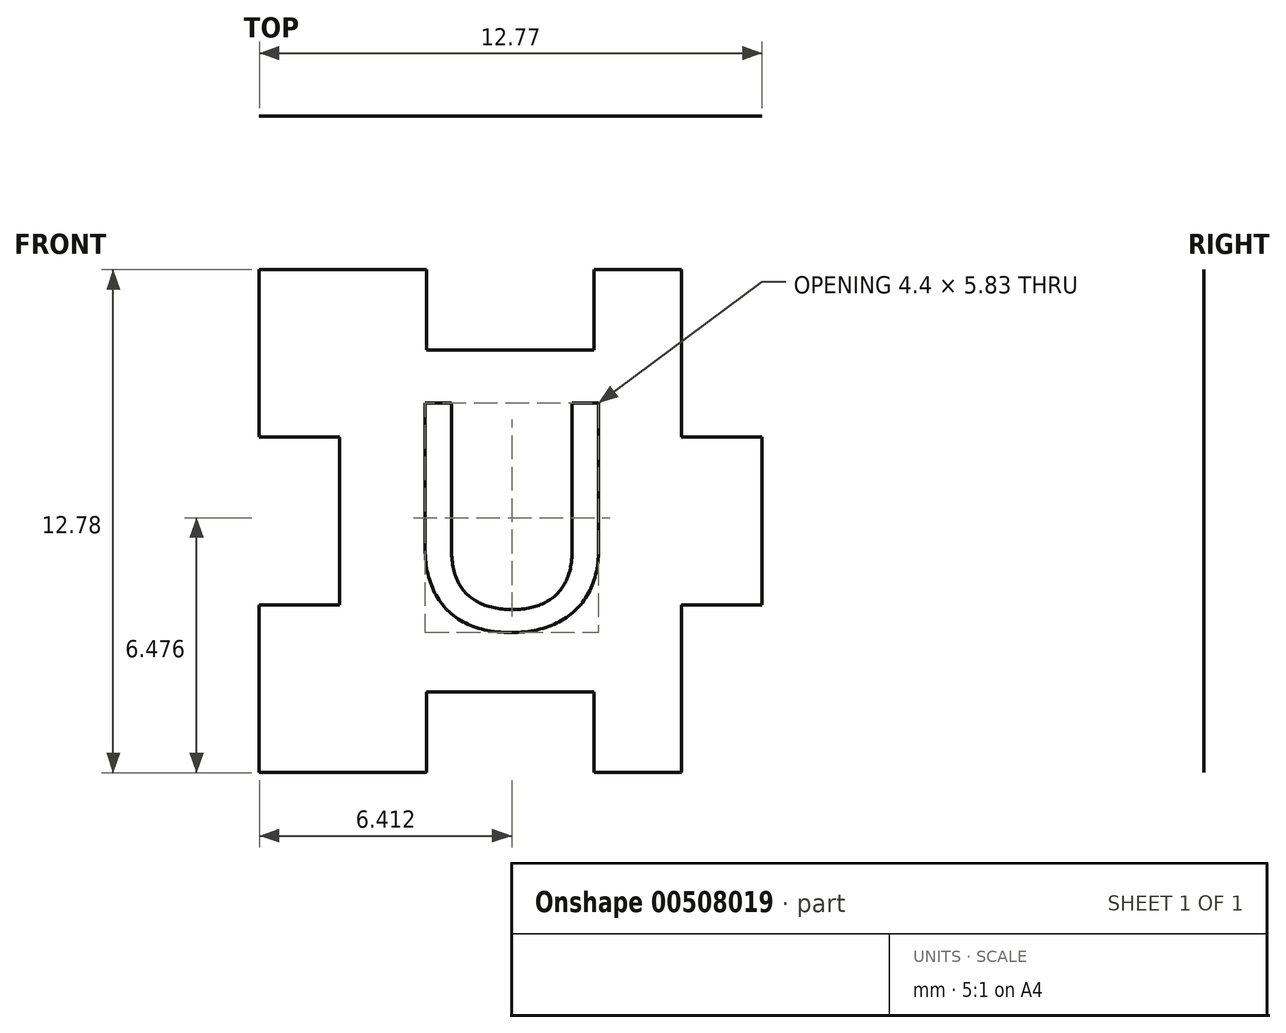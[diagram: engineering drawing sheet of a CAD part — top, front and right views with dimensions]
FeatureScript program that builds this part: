
annotation { "Feature Type Name" : "Feature", "Feature Type Description" : "" }
export const myFeature = defineFeature(function(context is Context, id is Id, definition is map)
    precondition{}
    {
        {
            var Q0;
            Q0=qCreatedBy(makeId("Front.planeOp"),FACE);
            var sketch = newSketch(context, id + "F0", { "sketchPlane" : qUnion([Q0])});
            skLineSegment(sketch, "E0", {"start": v(-10.99, 26.89) * mm, "end": v(-10.99, 29.02) * mm});
            skLineSegment(sketch, "E1", {"start": v(-10.99, 29.02) * mm, "end": v(-13.03, 29.02) * mm});
            skLineSegment(sketch, "E2", {"start": v(-13.03, 29.02) * mm, "end": v(-13.03, 33.28) * mm});
            skLineSegment(sketch, "E3", {"start": v(-13.03, 33.28) * mm, "end": v(-8.78, 33.28) * mm});
            skLineSegment(sketch, "E4", {"start": v(-8.78, 33.28) * mm, "end": v(-8.78, 31.23) * mm});
            skLineSegment(sketch, "E5", {"start": v(-8.78, 31.23) * mm, "end": v(-4.53, 31.23) * mm});
            skLineSegment(sketch, "E6", {"start": v(-4.53, 31.23) * mm, "end": v(-4.53, 33.28) * mm});
            skLineSegment(sketch, "E7", {"start": v(-4.53, 33.28) * mm, "end": v(-2.3, 33.28) * mm});
            skLineSegment(sketch, "E8", {"start": v(-2.3, 33.28) * mm, "end": v(-2.3, 29.02) * mm});
            skLineSegment(sketch, "E9", {"start": v(-2.3, 29.02) * mm, "end": v(-0.26, 29.02) * mm});
            skLineSegment(sketch, "E10", {"start": v(-10.99, 26.89) * mm, "end": v(8.72, 26.89) * mm, "construction": true});
            skLineSegment(sketch, "E11.MirrorCS", {"start": v(-2.3, 24.76) * mm, "end": v(-0.26, 24.76) * mm});
            skLineSegment(sketch, "E12.MirrorCS", {"start": v(-2.3, 20.5) * mm, "end": v(-2.3, 24.76) * mm});
            skLineSegment(sketch, "E13.MirrorCS", {"start": v(-4.53, 20.5) * mm, "end": v(-2.3, 20.5) * mm});
            skLineSegment(sketch, "E14.MirrorCS", {"start": v(-4.53, 22.55) * mm, "end": v(-4.53, 20.5) * mm});
            skLineSegment(sketch, "E15.MirrorCS", {"start": v(-8.78, 22.55) * mm, "end": v(-4.53, 22.55) * mm});
            skLineSegment(sketch, "E16.MirrorCS", {"start": v(-8.78, 20.5) * mm, "end": v(-8.78, 22.55) * mm});
            skLineSegment(sketch, "E17.MirrorCS", {"start": v(-13.03, 20.5) * mm, "end": v(-8.78, 20.5) * mm});
            skLineSegment(sketch, "E18.MirrorCS", {"start": v(-13.03, 24.76) * mm, "end": v(-13.03, 20.5) * mm});
            skLineSegment(sketch, "E19.MirrorCS", {"start": v(-10.99, 24.76) * mm, "end": v(-13.03, 24.76) * mm});
            skLineSegment(sketch, "E20.MirrorCS", {"start": v(-10.99, 26.89) * mm, "end": v(-10.99, 24.76) * mm});
            skLineSegment(sketch, "E21", {"start": v(-0.26, 29.02) * mm, "end": v(-0.26, 24.76) * mm});
            skSolve(sketch);
        }
        {
            var Q0;
            Q0=makeQuery(id+"F0.imprint","IMPRINT",FACE,{"disambiguationData":[TD([[makeQuery(id+"F0.imprint","IMPRINT",EDGE,{"derivedFrom":sQuery(id+"F0.wireOp",EDGE,"E0")}),-1.0]])]});
            extrude(context, id + "F1", {"entities" : qUnion([Q0]), "depth" : .16 / 50.8 * mm, "offsetDistance" : 25 * mm});
        }
        {
            var Q0;
            Q0=makeQuery(id+"F1.opExtrude","CAP_FACE",FACE,{"disambiguationData":[OSD([sQuery(id+"F0.wireOp",EDGE,"E0"),sQuery(id+"F0.wireOp",EDGE,"E1"),sQuery(id+"F0.wireOp",EDGE,"E2"),sQuery(id+"F0.wireOp",EDGE,"E3"),sQuery(id+"F0.wireOp",EDGE,"E4"),sQuery(id+"F0.wireOp",EDGE,"E5"),sQuery(id+"F0.wireOp",EDGE,"E6"),sQuery(id+"F0.wireOp",EDGE,"E7"),sQuery(id+"F0.wireOp",EDGE,"E8"),sQuery(id+"F0.wireOp",EDGE,"E9"),sQuery(id+"F0.wireOp",EDGE,"E11.MirrorCS"),sQuery(id+"F0.wireOp",EDGE,"E12.MirrorCS"),sQuery(id+"F0.wireOp",EDGE,"E13.MirrorCS"),sQuery(id+"F0.wireOp",EDGE,"E14.MirrorCS"),sQuery(id+"F0.wireOp",EDGE,"E15.MirrorCS"),sQuery(id+"F0.wireOp",EDGE,"E16.MirrorCS"),sQuery(id+"F0.wireOp",EDGE,"E17.MirrorCS"),sQuery(id+"F0.wireOp",EDGE,"E18.MirrorCS"),sQuery(id+"F0.wireOp",EDGE,"E19.MirrorCS"),sQuery(id+"F0.wireOp",EDGE,"E20.MirrorCS"),sQuery(id+"F0.wireOp",EDGE,"E21")])],"isStart":false});
            var sketch = newSketch(context, id + "F2", { "sketchPlane" : qUnion([Q0])});
            skText(sketch, "E22", { "text": "U", "fontName": "OpenSans-Regular.ttf"});
            const initialGuessF2  = {"E22": [-0.00955, 0.02414, 1, 0, 0.0058]};
            skSetInitialGuess(sketch, initialGuessF2);
            skSolve(sketch);
        }
        {
            var Q0;
            Q0=makeQuery(id+"F2.imprint","IMPRINT",FACE,{"disambiguationData":[TD([[makeQuery(id+"F2.imprint","IMPRINT",EDGE,{"derivedFrom":sQuery(id+"F2.wireOp",EDGE,"E22.sketch_text.stroke-0")}),-1.0]])]});
            extrude(context, id + "F3", {"entities" : qUnion([Q0]), "operationType" : NewBodyOperationType.REMOVE, "oppositeDirection" : true, "depth" : 1 * mm, "offsetDistance" : 25 * mm});
        }
    });
